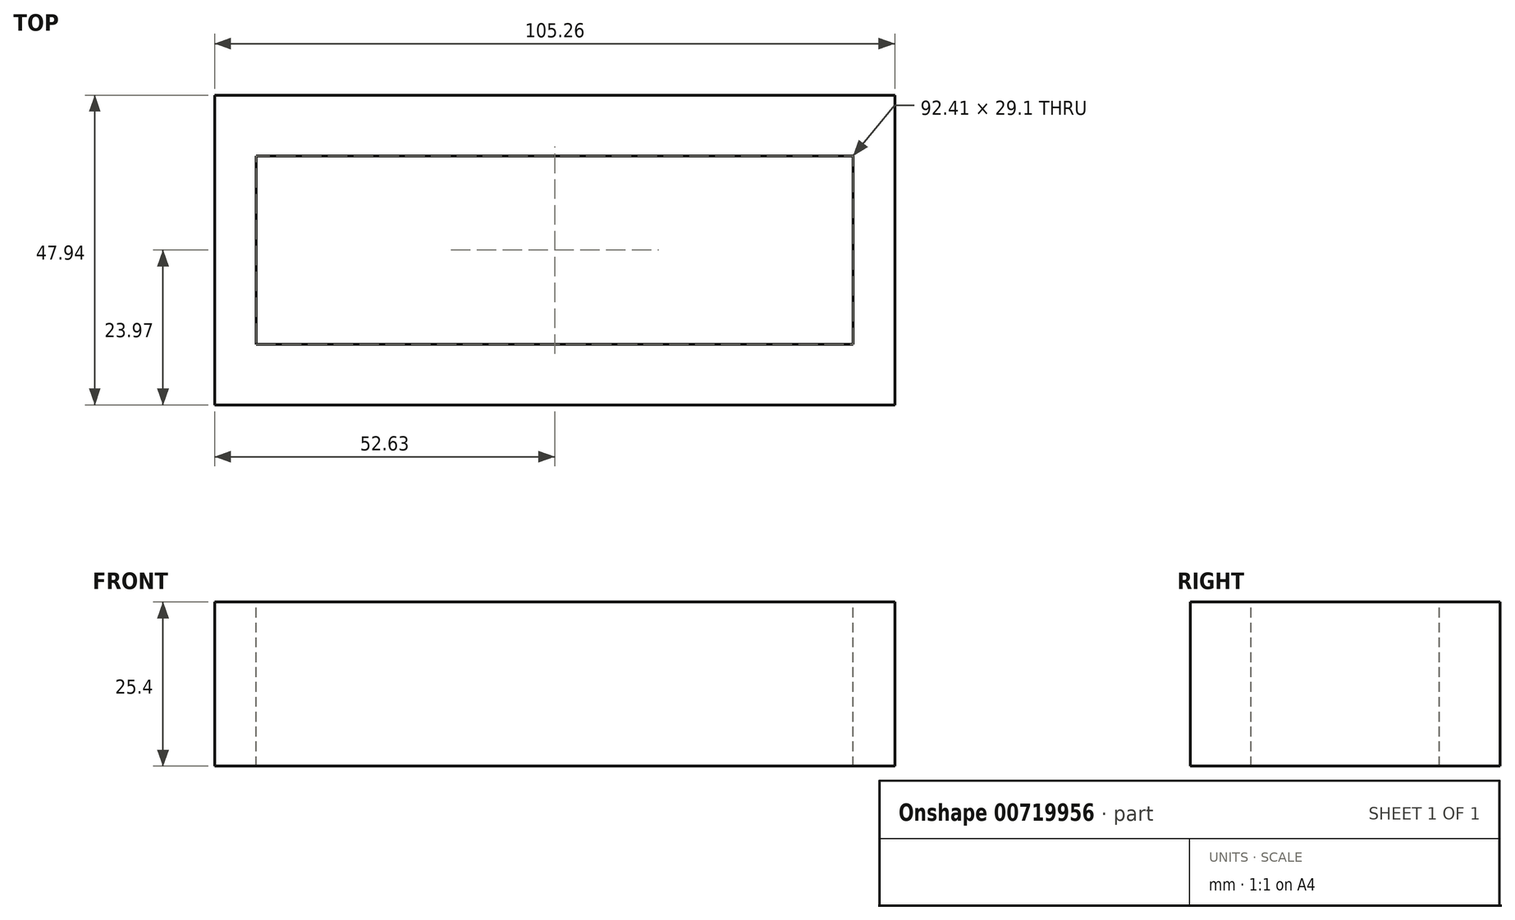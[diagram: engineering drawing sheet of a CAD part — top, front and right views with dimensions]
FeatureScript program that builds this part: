
annotation { "Feature Type Name" : "Feature", "Feature Type Description" : "" }
export const myFeature = defineFeature(function(context is Context, id is Id, definition is map)
    precondition{}
    {
        {
            var Q0;
            Q0=qCreatedBy(makeId("Top.planeOp"),FACE);
            var sketch = newSketch(context, id + "F0", { "sketchPlane" : qUnion([Q0])});
            skLineSegment(sketch, "E0.bottom", {"start": v(52.63, -23.97) * mm, "end": v(-52.63, -23.97) * mm});
            skLineSegment(sketch, "E0.top", {"start": v(52.63, 23.97) * mm, "end": v(-52.63, 23.97) * mm});
            skLineSegment(sketch, "E0.left", {"start": v(52.63, -23.97) * mm, "end": v(52.63, 23.97) * mm});
            skLineSegment(sketch, "E0.right", {"start": v(-52.63, -23.97) * mm, "end": v(-52.63, 23.97) * mm});
            skPoint(sketch, "E0.middle", {"position": v(0, 0) * mm});
            skSolve(sketch);
        }
        {
            var Q0;
            Q0 = qSketchRegion(id + "F0", true);
            extrude(context, id + "F1", {"entities" : qUnion([Q0]), "depth" : 25.4 * mm, "offsetDistance" : 25.4 * mm});
        }
        {
            var Q0;
            Q0=makeQuery(id+"F1.opExtrude","CAP_FACE",FACE,{"disambiguationData":[OSD([sQuery(id+"F0.wireOp",EDGE,"E0.bottom"),sQuery(id+"F0.wireOp",EDGE,"E0.top"),sQuery(id+"F0.wireOp",EDGE,"E0.left"),sQuery(id+"F0.wireOp",EDGE,"E0.right")])],"isStart":false});
            var sketch = newSketch(context, id + "F2", { "sketchPlane" : qUnion([Q0])});
            skLineSegment(sketch, "E1.bottom", {"start": v(46.2, 14.55) * mm, "end": v(-46.2, 14.55) * mm});
            skLineSegment(sketch, "E1.top", {"start": v(46.2, -14.55) * mm, "end": v(-46.2, -14.55) * mm});
            skLineSegment(sketch, "E1.left", {"start": v(46.2, 14.55) * mm, "end": v(46.2, -14.55) * mm});
            skLineSegment(sketch, "E1.right", {"start": v(-46.2, 14.55) * mm, "end": v(-46.2, -14.55) * mm});
            skPoint(sketch, "E1.middle", {"position": v(0, 0) * mm});
            skSolve(sketch);
        }
        {
            var Q0;
            Q0=makeQuery(id+"F2.imprint","IMPRINT",FACE,{"disambiguationData":[TD([[makeQuery(id+"F2.imprint","IMPRINT",EDGE,{"derivedFrom":sQuery(id+"F2.wireOp",EDGE,"E1.bottom")}),1.0]])]});
            extrude(context, id + "F3", {"entities" : qUnion([Q0]), "operationType" : NewBodyOperationType.REMOVE, "oppositeDirection" : true, "depth" : 25.4 * mm, "offsetDistance" : 25.4 * mm});
        }
    });
